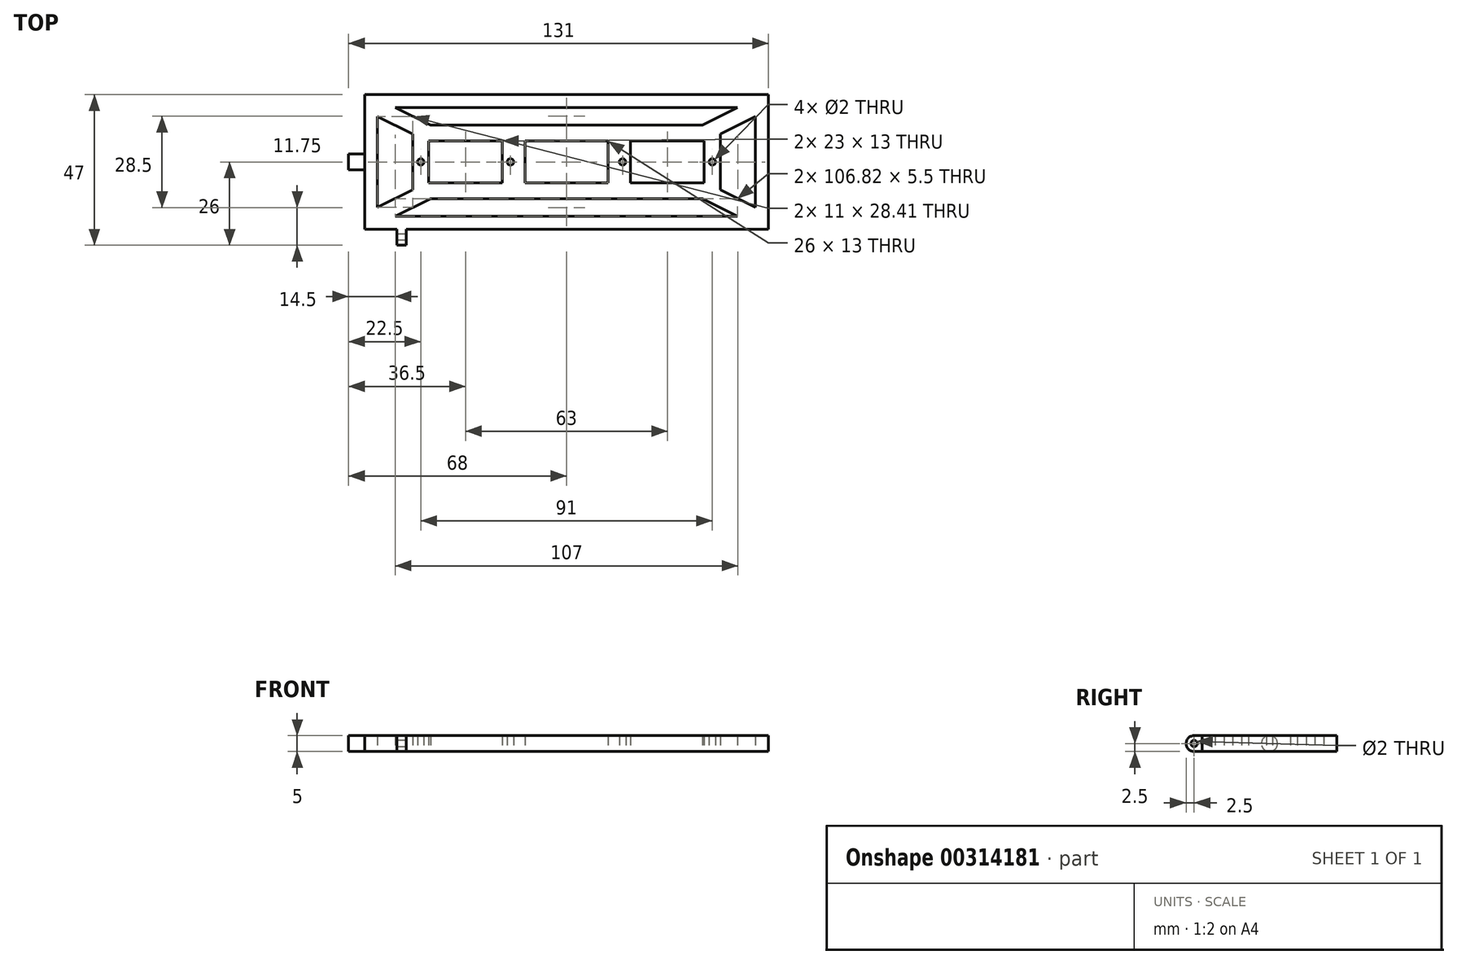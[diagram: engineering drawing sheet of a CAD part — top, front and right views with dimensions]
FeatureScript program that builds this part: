
annotation { "Feature Type Name" : "Feature", "Feature Type Description" : "" }
export const myFeature = defineFeature(function(context is Context, id is Id, definition is map)
    precondition{}
    {
        {
            var Q0;
            Q0=qCreatedBy(makeId("Top.planeOp"),FACE);
            var sketch = newSketch(context, id + "F0", { "sketchPlane" : qUnion([Q0])});
            skLineSegment(sketch, "E0.bottom", {"start": v(-63, 21) * mm, "end": v(63, 21) * mm});
            skLineSegment(sketch, "E0.top", {"start": v(-63, -21) * mm, "end": v(63, -21) * mm});
            skLineSegment(sketch, "E0.left", {"start": v(-63, 21) * mm, "end": v(-63, -21) * mm});
            skLineSegment(sketch, "E0.right", {"start": v(63, 21) * mm, "end": v(63, -21) * mm});
            skPoint(sketch, "E1", {"position": v(0, 21) * mm});
            skPoint(sketch, "E2", {"position": v(63, 0) * mm});
            skLineSegment(sketch, "E3.bottom", {"start": v(20, 6.5) * mm, "end": v(43, 6.5) * mm});
            skLineSegment(sketch, "E3.top", {"start": v(20, -6.5) * mm, "end": v(43, -6.5) * mm});
            skLineSegment(sketch, "E3.left", {"start": v(20, 6.5) * mm, "end": v(20, -6.5) * mm});
            skLineSegment(sketch, "E3.right", {"start": v(43, 6.5) * mm, "end": v(43, -6.5) * mm});
            skPoint(sketch, "E4", {"position": v(20, 0) * mm});
            skLineSegment(sketch, "E5.MirrorCS", {"start": v(-20, 6.5) * mm, "end": v(-20, -6.5) * mm});
            skLineSegment(sketch, "E6.MirrorCS", {"start": v(-20, 6.5) * mm, "end": v(-43, 6.5) * mm});
            skLineSegment(sketch, "E7.MirrorCS", {"start": v(-43, 6.5) * mm, "end": v(-43, -6.5) * mm});
            skLineSegment(sketch, "E8.MirrorCS", {"start": v(-20, -6.5) * mm, "end": v(-43, -6.5) * mm});
            skCircle(sketch, "E9", {"center": v(17.5, 0) * mm, "radius": 1 * mm});
            skCircle(sketch, "E10", {"center": v(45.5, 0) * mm, "radius": 1 * mm});
            skLineSegment(sketch, "E11", {"start": v(17.5, 0) * mm, "end": v(20, 0) * mm, "construction": true});
            skLineSegment(sketch, "E12", {"start": v(45.5, 0) * mm, "end": v(43, 0) * mm, "construction": true});
            skCircle(sketch, "E13.MirrorC", {"center": v(-17.5, 0) * mm, "radius": 1 * mm});
            skCircle(sketch, "E14.MirrorC", {"center": v(-45.5, 0) * mm, "radius": 1 * mm});
            skLineSegment(sketch, "E15.0", {"start": v(7, 11.5) * mm, "end": v(42.4, 11.5) * mm});
            skLineSegment(sketch, "E15.2", {"start": v(7, -11.5) * mm, "end": v(42.4, -11.5) * mm});
            skLineSegment(sketch, "E15.3", {"start": v(48, 8.7) * mm, "end": v(48, -8.7) * mm});
            skLineSegment(sketch, "E16.MirrorCS", {"start": v(-7, 11.5) * mm, "end": v(-42.4, 11.5) * mm});
            skLineSegment(sketch, "E17.MirrorCS", {"start": v(-48, 8.7) * mm, "end": v(-48, -8.7) * mm});
            skLineSegment(sketch, "E18.MirrorCS", {"start": v(-7, -11.5) * mm, "end": v(-42.4, -11.5) * mm});
            skLineSegment(sketch, "E19", {"start": v(-7, 11.5) * mm, "end": v(7, 11.5) * mm});
            skLineSegment(sketch, "E20", {"start": v(-7, -11.5) * mm, "end": v(7, -11.5) * mm});
            skLineSegment(sketch, "E21.bottom", {"start": v(-13, 6.5) * mm, "end": v(13, 6.5) * mm});
            skLineSegment(sketch, "E21.top", {"start": v(-13, -6.5) * mm, "end": v(13, -6.5) * mm});
            skLineSegment(sketch, "E21.left", {"start": v(-13, 6.5) * mm, "end": v(-13, -6.5) * mm});
            skLineSegment(sketch, "E21.right", {"start": v(13, 6.5) * mm, "end": v(13, -6.5) * mm});
            skLineSegment(sketch, "E22.0", {"start": v(-53.4, 17) * mm, "end": v(53.4, 17) * mm});
            skLineSegment(sketch, "E22.1", {"start": v(-59, 14.2) * mm, "end": v(-59, -14.2) * mm});
            skLineSegment(sketch, "E22.2", {"start": v(-53.4, -17) * mm, "end": v(53.4, -17) * mm});
            skLineSegment(sketch, "E22.3", {"start": v(59, 14.2) * mm, "end": v(59, -14.2) * mm});
            skLineSegment(sketch, "E23", {"start": v(-59, 17) * mm, "end": v(-48, 11.5) * mm, "construction": true});
            skLineSegment(sketch, "E24.0", {"start": v(-59, 14.2) * mm, "end": v(-48, 8.7) * mm});
            skLineSegment(sketch, "E25.0", {"start": v(-53.4, 17) * mm, "end": v(-42.4, 11.5) * mm});
            skLineSegment(sketch, "E26.MirrorCS", {"start": v(53.4, 17) * mm, "end": v(42.4, 11.5) * mm});
            skLineSegment(sketch, "E27.MirrorCS", {"start": v(59, 14.2) * mm, "end": v(48, 8.7) * mm});
            skLineSegment(sketch, "E28.MirrorCS", {"start": v(59, -14.2) * mm, "end": v(48, -8.7) * mm});
            skLineSegment(sketch, "E29.MirrorCS", {"start": v(53.4, -17) * mm, "end": v(42.4, -11.5) * mm});
            skLineSegment(sketch, "E30.MirrorCS", {"start": v(-53.4, -17) * mm, "end": v(-42.4, -11.5) * mm});
            skLineSegment(sketch, "E31.MirrorCS", {"start": v(-59, -14.2) * mm, "end": v(-48, -8.7) * mm});
            skPoint(sketch, "E32.orphan", {"position": v(-48, 11.5) * mm});
            skPoint(sketch, "E33.orphan", {"position": v(48, 11.5) * mm});
            skPoint(sketch, "E34.orphan", {"position": v(48, -11.5) * mm});
            skPoint(sketch, "E35.orphan", {"position": v(-48, -11.5) * mm});
            skSolve(sketch);
        }
        {
            var Q0;
            Q0=makeQuery(id+"F0.imprint","IMPRINT",FACE,{"disambiguationData":[TD([[makeQuery(id+"F0.imprint","IMPRINT",EDGE,{"derivedFrom":sQuery(id+"F0.wireOp",EDGE,"E0.bottom")}),-1.0]])]});
            extrude(context, id + "F1", {"entities" : qUnion([Q0]), "depth" : 5 * mm});
        }
        {
            var Q0;
            Q0=makeQuery(id+"F1.opExtrude","SWEPT_FACE",FACE,{"disambiguationData":[OSD([sQuery(id+"F0.wireOp",EDGE,"E0.left")])]});
            var sketch = newSketch(context, id + "F2", { "sketchPlane" : qUnion([Q0])});
            skCircle(sketch, "E36", {"center": v(0, 2.5) * mm, "radius": 2.5 * mm});
            skSolve(sketch);
        }
        {
            var Q0;
            {var subQ0=sQuery(id+"F2.wireOp",EDGE,"E36");var subQ1=sQuery(id+"F0.wireOp",EDGE,"E0.left");var subQ2=makeQuery(id+"F2.imprint","INTERSECT",VERTEX,{"derivedFrom":[makeQuery(id+"F1.opExtrude","CAP_EDGE",EDGE,{"disambiguationData":[OSD([subQ1])],"isStart":true}),subQ0]});Q0=makeQuery(id+"F2.imprint","IMPRINT",FACE,{"disambiguationData":[TD([[makeQuery(id+"F2.imprint","IMPRINT",EDGE,{"disambiguationData":[TD([[subQ2,1.0]])],"derivedFrom":subQ0}),1.0]])]});}
            extrude(context, id + "F3", {"entities" : qUnion([Q0]), "operationType" : NewBodyOperationType.ADD, "depth" : 5 * mm});
        }
        {
            var Q0;
            Q0=makeQuery(id+"F1.opExtrude","SWEPT_FACE",FACE,{"disambiguationData":[OSD([sQuery(id+"F0.wireOp",EDGE,"E0.top")])]});
            var sketch = newSketch(context, id + "F4", { "sketchPlane" : qUnion([Q0])});
            skLineSegment(sketch, "E37.0", {"start": v(-63, 5) * mm, "end": v(63, 5) * mm});
            skLineSegment(sketch, "E37.1", {"start": v(-63, 0) * mm, "end": v(63, 0) * mm});
            skLineSegment(sketch, "E37.2", {"start": v(-63, 5) * mm, "end": v(-63, 0) * mm});
            skLineSegment(sketch, "E37.3", {"start": v(63, 5) * mm, "end": v(63, 0) * mm});
            skLineSegment(sketch, "E38", {"start": v(-53, 5) * mm, "end": v(-53, 0) * mm});
            skLineSegment(sketch, "E39", {"start": v(-50, 5) * mm, "end": v(-50, 0) * mm});
            skSolve(sketch);
        }
        {
            var Q0;
            {var subQ0=sQuery(id+"F4.wireOp",EDGE,"E38");Q0=makeQuery(id+"F4.imprint","IMPRINT",FACE,{"disambiguationData":[TD([[makeQuery(id+"F4.imprint","IMPRINT",EDGE,{"derivedFrom":subQ0}),1.0]])]});}
            extrude(context, id + "F5", {"entities" : qUnion([Q0]), "operationType" : NewBodyOperationType.ADD, "depth" : 5 * mm});
        }
        {
            var Q0;
            Q0=makeQuery(id+"F5.opExtrude","SWEPT_FACE",FACE,{"disambiguationData":[OSD([sQuery(id+"F4.wireOp",EDGE,"E38")])]});
            var sketch = newSketch(context, id + "F6", { "sketchPlane" : qUnion([Q0])});
            skLineSegment(sketch, "E40.0", {"start": v(26, 5) * mm, "end": v(23.5, 5) * mm});
            skLineSegment(sketch, "E40.1", {"start": v(26, 5) * mm, "end": v(26, 0) * mm});
            skLineSegment(sketch, "E40.2", {"start": v(26, 0) * mm, "end": v(23.5, 0) * mm});
            skArc(sketch, "E41", {"start": v(23.5, 0) * mm, "mid": v(26, 2.5) * mm, "end": v(23.5, 5) * mm});
            skPoint(sketch, "E42.orphan", {"position": v(21, 5) * mm});
            skPoint(sketch, "E43.orphan", {"position": v(21, 0) * mm});
            skCircle(sketch, "E44", {"center": v(23.5, 2.5) * mm, "radius": 1 * mm});
            skSolve(sketch);
        }
        {
            var Q0;
            Q0=makeQuery(id+"F6.imprint","IMPRINT",FACE,{"disambiguationData":[TD([[makeQuery(id+"F6.imprint","IMPRINT",EDGE,{"derivedFrom":sQuery(id+"F6.wireOp",EDGE,"E44")}),1.0]])]});
            var Q1;
            {var subQ0=sQuery(id+"F6.wireOp",EDGE,"E40.0");Q1=makeQuery(id+"F6.imprint","IMPRINT",FACE,{"disambiguationData":[TD([[makeQuery(id+"F6.imprint","IMPRINT",EDGE,{"derivedFrom":subQ0}),1.0]])]});}
            var Q2;
            {var subQ0=sQuery(id+"F6.wireOp",EDGE,"E40.2");Q2=makeQuery(id+"F6.imprint","IMPRINT",FACE,{"disambiguationData":[TD([[makeQuery(id+"F6.imprint","IMPRINT",EDGE,{"derivedFrom":subQ0}),-1.0]])]});}
            var Q3;
            Q3=makeQuery(id+"F5.opExtrude","SWEPT_FACE",FACE,{"disambiguationData":[OSD([sQuery(id+"F4.wireOp",EDGE,"E39")])]});
            extrude(context, id + "F7", {"entities" : qUnion([Q0, Q1, Q2]), "operationType" : NewBodyOperationType.REMOVE, "endBound" : BoundingType.UP_TO_SURFACE, "oppositeDirection" : true, "endBoundEntityFace" : qUnion([Q3]), "depth" : 25 * mm});
        }
    });
